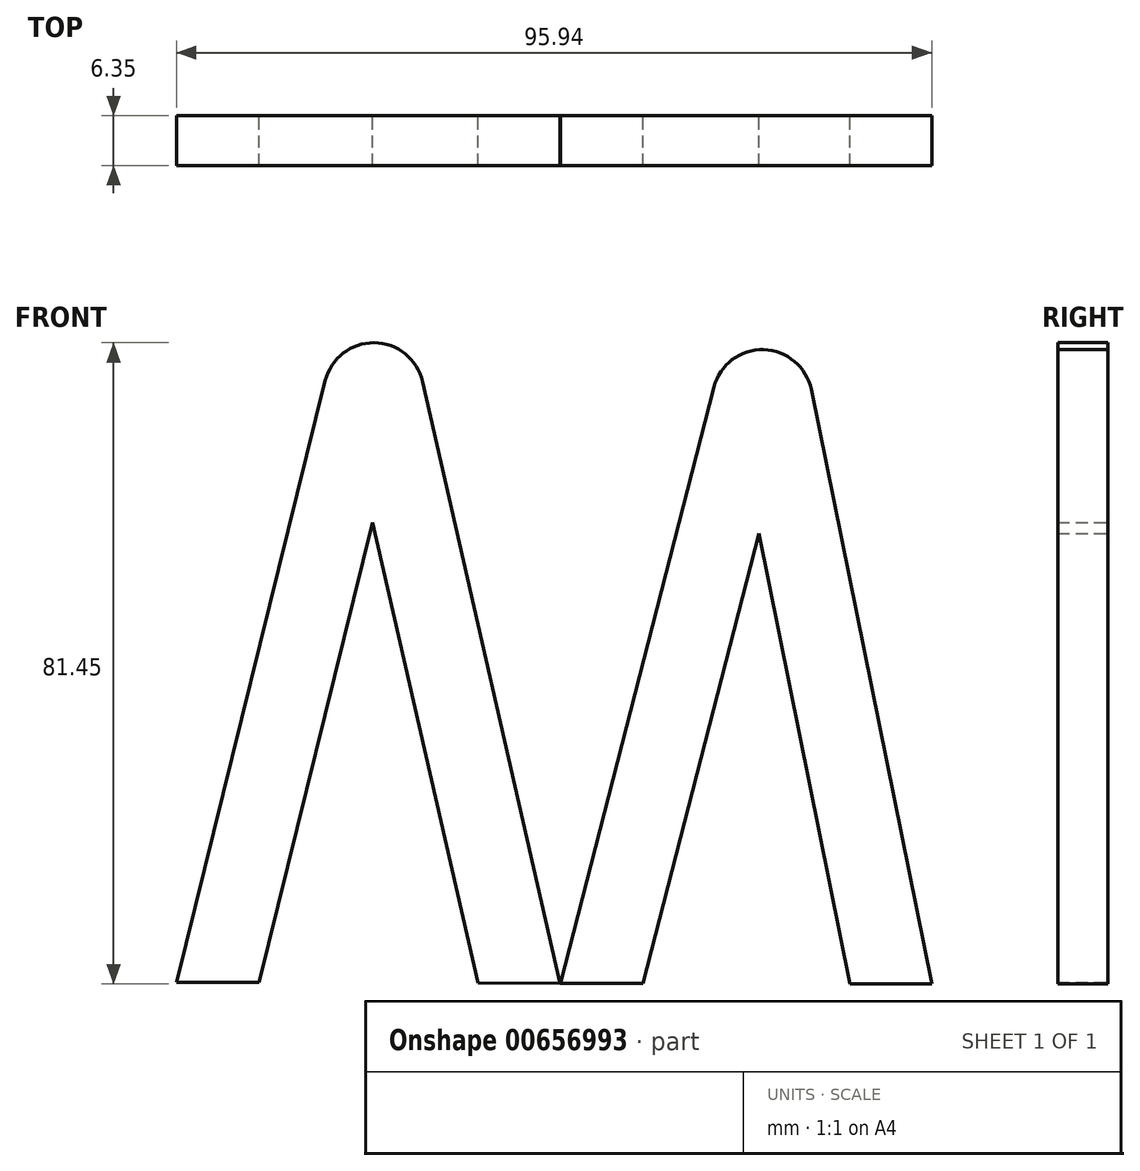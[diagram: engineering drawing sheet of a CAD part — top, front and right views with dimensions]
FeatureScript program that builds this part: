
annotation { "Feature Type Name" : "Feature", "Feature Type Description" : "" }
export const myFeature = defineFeature(function(context is Context, id is Id, definition is map)
    precondition{}
    {
        {
            var Q0;
            Q0=qCreatedBy(makeId("Front.planeOp"),FACE);
            var sketch = newSketch(context, id + "F0", { "sketchPlane" : qUnion([Q0])});
            skLineSegment(sketch, "E0", {"start": v(-47.54, -55.5) * mm, "end": v(-28.64, 20.92) * mm});
            skLineSegment(sketch, "E1", {"start": v(-16.29, 20.81) * mm, "end": v(1.2, -55.7) * mm});
            skLineSegment(sketch, "E2", {"start": v(1.2, -55.7) * mm, "end": v(20.73, 20.1) * mm});
            skLineSegment(sketch, "E3", {"start": v(33.1, 19.78) * mm, "end": v(48.4, -55.7) * mm});
            skArc(sketch, "E4.filletArc", {"start": v(-16.29, 20.81) * mm, "mid": v(-22.42, 25.75) * mm, "end": v(-28.64, 20.92) * mm});
            skArc(sketch, "E5.filletArc", {"start": v(33.1, 19.78) * mm, "mid": v(27.04, 24.86) * mm, "end": v(20.73, 20.1) * mm});
            skLineSegment(sketch, "E6.0", {"start": v(26.43, 1.53) * mm, "end": v(38.03, -55.68) * mm});
            skLineSegment(sketch, "E6.1", {"start": v(11.71, -55.63) * mm, "end": v(26.43, 1.53) * mm});
            skLineSegment(sketch, "E6.2", {"start": v(-22.62, 2.93) * mm, "end": v(-9.25, -55.58) * mm});
            skLineSegment(sketch, "E6.3", {"start": v(-37.08, -55.52) * mm, "end": v(-22.62, 2.93) * mm});
            skLineSegment(sketch, "E7", {"start": v(-47.54, -55.5) * mm, "end": v(-37.08, -55.52) * mm});
            skLineSegment(sketch, "E8.trimOffspring", {"start": v(-9.25, -55.58) * mm, "end": v(11.71, -55.63) * mm});
            skLineSegment(sketch, "E9.trimOffspring", {"start": v(38.03, -55.68) * mm, "end": v(48.4, -55.7) * mm});
            skSolve(sketch);
        }
        {
            var Q0;
            Q0 = qSketchRegion(id + "F0", true);
            extrude(context, id + "F1", {"entities" : qUnion([Q0]), "depth" : 6.35 * mm, "offsetDistance" : 25.4 * mm});
        }
    });
